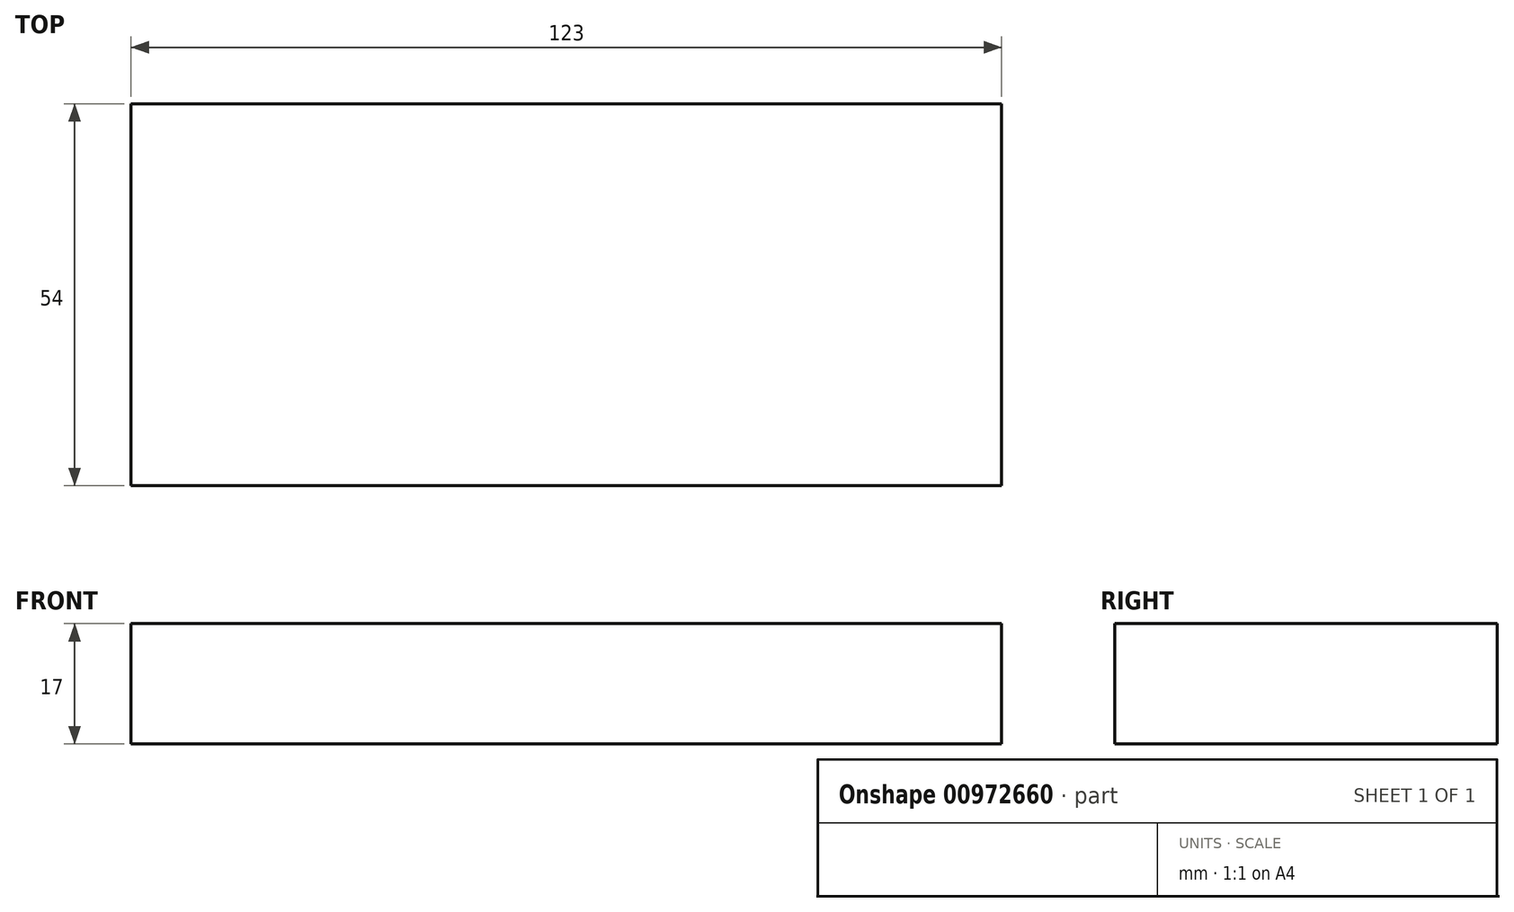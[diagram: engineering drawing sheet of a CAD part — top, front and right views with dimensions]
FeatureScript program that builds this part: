
annotation { "Feature Type Name" : "Feature", "Feature Type Description" : "" }
export const myFeature = defineFeature(function(context is Context, id is Id, definition is map)
    precondition{}
    {
        {
            var Q0;
            Q0=qCreatedBy(makeId("Top.planeOp"),FACE);
            var sketch = newSketch(context, id + "F0", { "sketchPlane" : qUnion([Q0])});
            skLineSegment(sketch, "E0.bottom", {"start": v(0, 54) * mm, "end": v(123, 54) * mm});
            skLineSegment(sketch, "E0.top", {"start": v(0, 0) * mm, "end": v(123, 0) * mm});
            skLineSegment(sketch, "E0.left", {"start": v(0, 54) * mm, "end": v(0, 0) * mm});
            skLineSegment(sketch, "E0.right", {"start": v(123, 54) * mm, "end": v(123, 0) * mm});
            skSolve(sketch);
        }
        {
            var Q0;
            Q0=makeQuery(id+"F0.imprint","IMPRINT",FACE,{"disambiguationData":[TD([[makeQuery(id+"F0.imprint","IMPRINT",EDGE,{"derivedFrom":sQuery(id+"F0.wireOp",EDGE,"E0.bottom")}),-1.0]])]});
            extrude(context, id + "F1", {"entities" : qUnion([Q0]), "depth" : 17 * mm, "offsetDistance" : 25 * mm});
        }
    });
